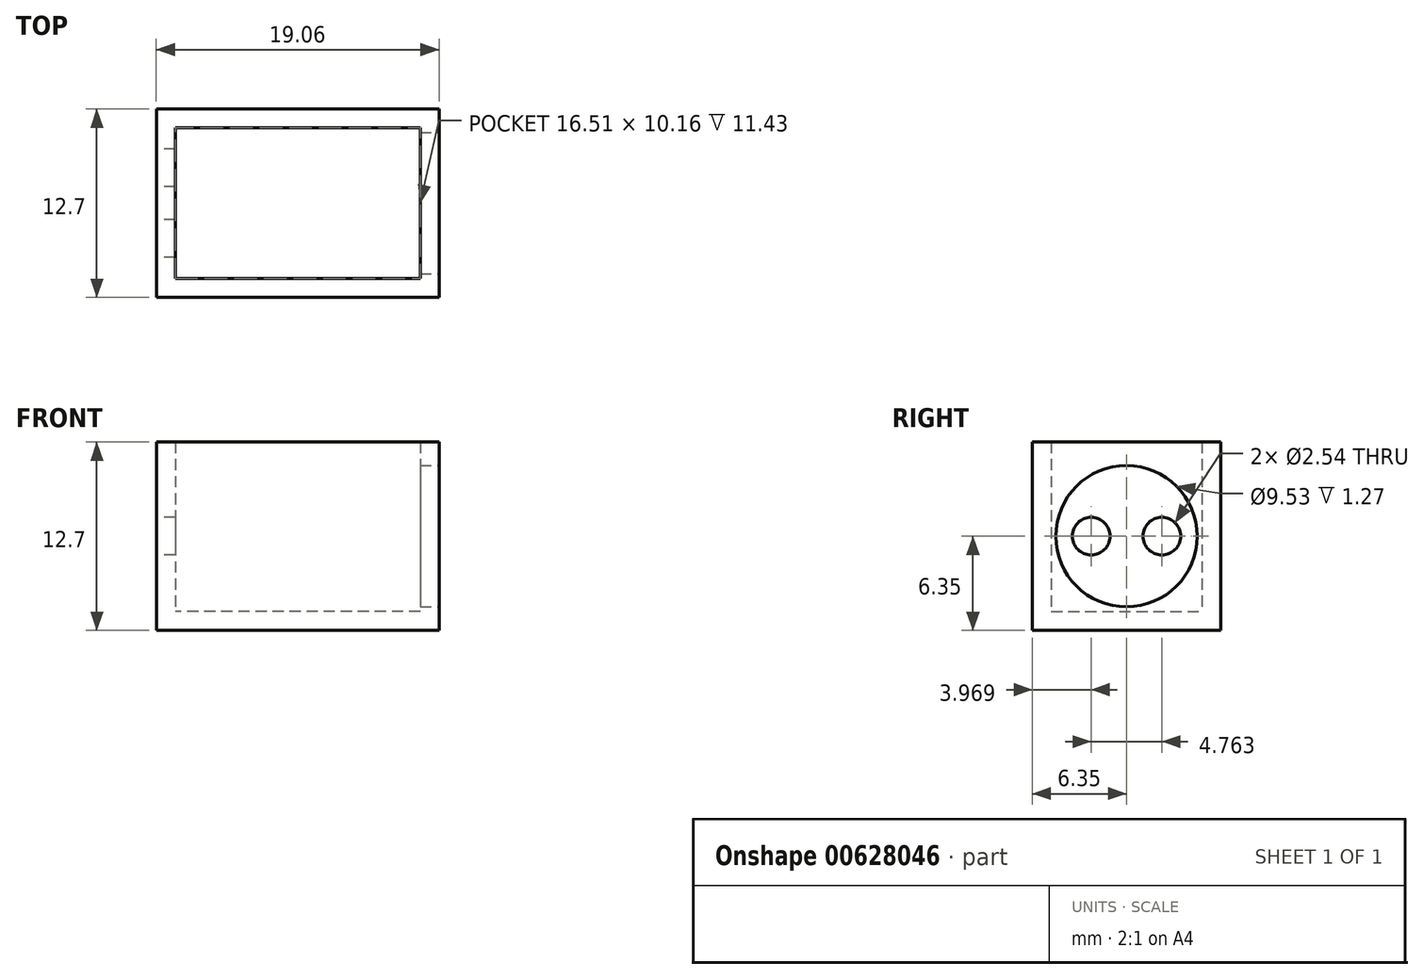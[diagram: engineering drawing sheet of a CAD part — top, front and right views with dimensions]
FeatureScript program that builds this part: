
annotation { "Feature Type Name" : "Feature", "Feature Type Description" : "" }
export const myFeature = defineFeature(function(context is Context, id is Id, definition is map)
    precondition{}
    {
        {
            var Q0;
            Q0=qCreatedBy(makeId("Top.planeOp"),FACE);
            var sketch = newSketch(context, id + "F0", { "sketchPlane" : qUnion([Q0])});
            skLineSegment(sketch, "E0.bottom", {"start": v(9.53, -6.35) * mm, "end": v(-9.53, -6.35) * mm});
            skLineSegment(sketch, "E0.top", {"start": v(9.53, 6.35) * mm, "end": v(-9.53, 6.35) * mm});
            skLineSegment(sketch, "E0.left", {"start": v(9.53, -6.35) * mm, "end": v(9.53, 6.35) * mm});
            skLineSegment(sketch, "E0.right", {"start": v(-9.53, -6.35) * mm, "end": v(-9.53, 6.35) * mm});
            skPoint(sketch, "E0.middle", {"position": v(0, 0) * mm});
            skSolve(sketch);
        }
        {
            var Q0;
            Q0 = qSketchRegion(id + "F0", true);
            extrude(context, id + "F1", {"entities" : qUnion([Q0]), "depth" : 12.7 * mm, "offsetDistance" : 25.4 * mm});
        }
        {
            var Q0;
            Q0=makeQuery(id+"F1.opExtrude","CAP_FACE",FACE,{"disambiguationData":[OSD([sQuery(id+"F0.wireOp",EDGE,"E0.bottom"),sQuery(id+"F0.wireOp",EDGE,"E0.top"),sQuery(id+"F0.wireOp",EDGE,"E0.left"),sQuery(id+"F0.wireOp",EDGE,"E0.right")])],"isStart":false});
            shell(context, id + "F2", {"entities" : qUnion([Q0]), "thickness" : 1.27 * mm});
        }
        {
            var Q0;
            Q0=makeQuery(id+"F1.opExtrude","SWEPT_FACE",FACE,{"disambiguationData":[OSD([sQuery(id+"F0.wireOp",EDGE,"E0.left")])]});
            var sketch = newSketch(context, id + "F3", { "sketchPlane" : qUnion([Q0])});
            skCircle(sketch, "E1", {"center": v(0, 6.35) * mm, "radius": 4.76 * mm});
            skSolve(sketch);
        }
        {
            var Q0;
            Q0 = qSketchRegion(id + "F3", true);
            extrude(context, id + "F4", {"entities" : qUnion([Q0]), "operationType" : NewBodyOperationType.REMOVE, "endBound" : BoundingType.UP_TO_NEXT, "oppositeDirection" : true, "depth" : 25.4 * mm, "offsetDistance" : 25.4 * mm});
        }
        {
            var Q0;
            Q0=makeQuery(id+"F1.opExtrude","SWEPT_FACE",FACE,{"disambiguationData":[OSD([sQuery(id+"F0.wireOp",EDGE,"E0.right")])]});
            var sketch = newSketch(context, id + "F5", { "sketchPlane" : qUnion([Q0])});
            skCircle(sketch, "E2", {"center": v(-2.38, 6.35) * mm, "radius": 1.27 * mm});
            skCircle(sketch, "E3", {"center": v(2.38, 6.35) * mm, "radius": 1.27 * mm});
            skLineSegment(sketch, "E4", {"start": v(-2.38, 6.35) * mm, "end": v(2.38, 6.35) * mm, "construction": true});
            skLineSegment(sketch, "E5", {"start": v(0, 0) * mm, "end": v(0, 6.35) * mm, "construction": true});
            skPoint(sketch, "E5.endSnap0", {"position": v(0, 0) * mm});
            skSolve(sketch);
        }
        {
            var Q0;
            Q0 = qSketchRegion(id + "F5", true);
            extrude(context, id + "F6", {"entities" : qUnion([Q0]), "operationType" : NewBodyOperationType.REMOVE, "endBound" : BoundingType.UP_TO_NEXT, "oppositeDirection" : true, "depth" : 25.4 * mm, "offsetDistance" : 25.4 * mm});
        }
    });
